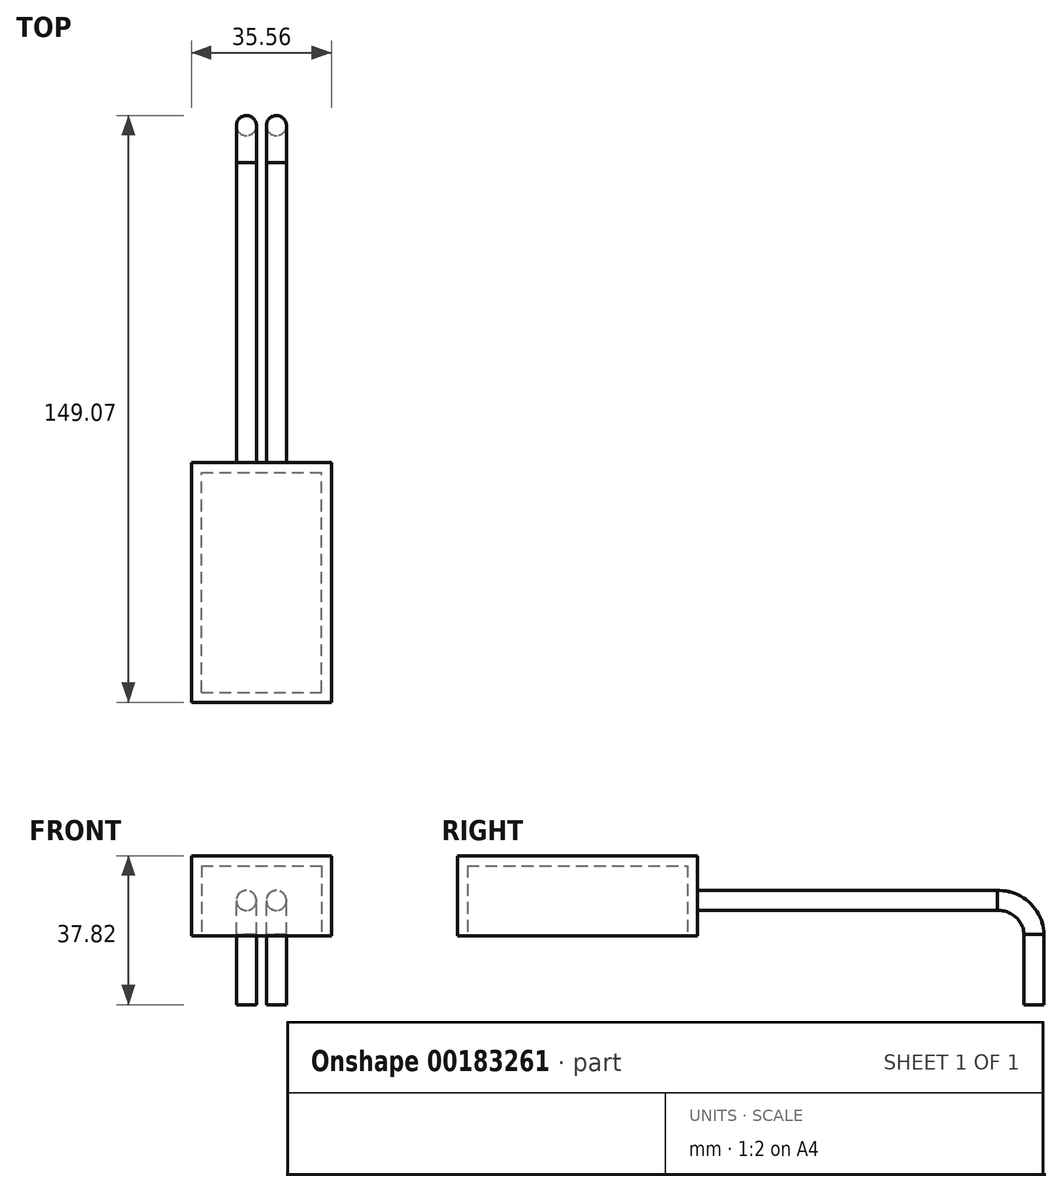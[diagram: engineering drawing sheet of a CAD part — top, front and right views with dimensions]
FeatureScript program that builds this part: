
annotation { "Feature Type Name" : "Feature", "Feature Type Description" : "" }
export const myFeature = defineFeature(function(context is Context, id is Id, definition is map)
    precondition{}
    {
        {
            var Q0;
            Q0=qCreatedBy(makeId("Top.planeOp"),FACE);
            var sketch = newSketch(context, id + "F0", { "sketchPlane" : qUnion([Q0])});
            skLineSegment(sketch, "E0.bottom", {"start": v(0, 0) * mm, "end": v(30.48, 0) * mm});
            skLineSegment(sketch, "E0.top", {"start": v(0, 55.88) * mm, "end": v(30.48, 55.88) * mm});
            skLineSegment(sketch, "E0.left", {"start": v(0, 0) * mm, "end": v(0, 55.88) * mm});
            skLineSegment(sketch, "E0.right", {"start": v(30.48, 0) * mm, "end": v(30.48, 55.88) * mm});
            skLineSegment(sketch, "E1.bottom", {"start": v(-2.54, -2.54) * mm, "end": v(33.02, -2.54) * mm});
            skLineSegment(sketch, "E1.top", {"start": v(-2.54, 58.42) * mm, "end": v(33.02, 58.42) * mm});
            skLineSegment(sketch, "E1.left", {"start": v(-2.54, -2.54) * mm, "end": v(-2.54, 58.42) * mm});
            skLineSegment(sketch, "E1.right", {"start": v(33.02, -2.54) * mm, "end": v(33.02, 58.42) * mm});
            skLineSegment(sketch, "E2.bottom", {"start": v(22.16, 0) * mm, "end": v(22.47, 0) * mm});
            skLineSegment(sketch, "E2.top", {"start": v(22.16, -2.54) * mm, "end": v(22.47, -2.54) * mm});
            skSolve(sketch);
        }
        {
            var Q0;
            Q0=makeQuery(id+"F0.imprint","IMPRINT",FACE,{"disambiguationData":[TD([[makeQuery(id+"F0.imprint","IMPRINT",EDGE,{"derivedFrom":sQuery(id+"F0.wireOp",EDGE,"E0.top")}),1.0]])]});
            extrude(context, id + "F1", {"entities" : qUnion([Q0]), "depth" : 20.32 * mm});
        }
        {
            var Q0;
            Q0=makeQuery(id+"F1.opExtrude","CAP_FACE",FACE,{"disambiguationData":[OSD([sQuery(id+"F0.wireOp",EDGE,"E0.bottom"),sQuery(id+"F0.wireOp",EDGE,"E0.top"),sQuery(id+"F0.wireOp",EDGE,"E0.left"),sQuery(id+"F0.wireOp",EDGE,"E0.right"),sQuery(id+"F0.wireOp",EDGE,"E1.bottom"),sQuery(id+"F0.wireOp",EDGE,"E1.top"),sQuery(id+"F0.wireOp",EDGE,"E1.left"),sQuery(id+"F0.wireOp",EDGE,"E1.right"),sQuery(id+"F0.wireOp",EDGE,"E2.bottom"),sQuery(id+"F0.wireOp",EDGE,"E2.top")])],"isStart":false});
            var sketch = newSketch(context, id + "F2", { "sketchPlane" : qUnion([Q0])});
            skLineSegment(sketch, "E3.bottom", {"start": v(-2.54, -2.54) * mm, "end": v(33.02, -2.54) * mm});
            skLineSegment(sketch, "E3.top", {"start": v(-2.54, 58.42) * mm, "end": v(33.02, 58.42) * mm});
            skLineSegment(sketch, "E3.left", {"start": v(-2.54, -2.54) * mm, "end": v(-2.54, 58.42) * mm});
            skLineSegment(sketch, "E3.right", {"start": v(33.02, -2.54) * mm, "end": v(33.02, 58.42) * mm});
            skSolve(sketch);
        }
        {
            var Q0;
            Q0=makeQuery(id+"F2.imprint","IMPRINT",FACE,{"disambiguationData":[TD([[makeQuery(id+"F2.imprint","IMPRINT",EDGE,{"derivedFrom":makeQuery(id+"F1.opExtrude","CAP_EDGE",EDGE,{"disambiguationData":[OSD([sQuery(id+"F0.wireOp",EDGE,"E0.top")])],"isStart":false})}),-1.0]])]});
            extrude(context, id + "F3", {"entities" : qUnion([Q0]), "operationType" : NewBodyOperationType.ADD, "oppositeDirection" : true, "depth" : 2.54 * mm});
        }
        {
            var Q0;
            Q0=makeQuery(id+"F1.opExtrude","SWEPT_FACE",FACE,{"disambiguationData":[OSD([sQuery(id+"F0.wireOp",EDGE,"E1.top")])]});
            var sketch = newSketch(context, id + "F4", { "sketchPlane" : qUnion([Q0])});
            skCircle(sketch, "E4", {"center": v(-11.43, 8.95) * mm, "radius": 2.54 * mm});
            skCircle(sketch, "E5", {"center": v(-19.05, 8.95) * mm, "radius": 2.54 * mm});
            skSolve(sketch);
        }
        {
            var Q0;
            Q0=qCreatedBy(makeId("Right.planeOp"),FACE);
            var sketch = newSketch(context, id + "F5", { "sketchPlane" : qUnion([Q0])});
            skLineSegment(sketch, "E6", {"start": v(58.83, 9.09) * mm, "end": v(135.03, 9.09) * mm});
            skLineSegment(sketch, "E7", {"start": v(135.03, 9.09) * mm, "end": v(135.03, 0) * mm, "construction": true});
            skArc(sketch, "E8", {"start": v(144.12, 0) * mm, "mid": v(141.46, 6.43) * mm, "end": v(135.03, 9.09) * mm});
            skLineSegment(sketch, "E9", {"start": v(144.12, 0) * mm, "end": v(144.12, -17.92) * mm});
            skLineSegment(sketch, "E10", {"start": v(58.42, 0) * mm, "end": v(58.42, 16.15) * mm, "construction": true});
            skLineSegment(sketch, "E11", {"start": v(58.83, 9.09) * mm, "end": v(58.42, 9.09) * mm});
            skSolve(sketch);
        }
        {
            var Q0;
            Q0=makeQuery(id+"F4.imprint","IMPRINT",FACE,{"disambiguationData":[TD([[makeQuery(id+"F4.imprint","IMPRINT",EDGE,{"derivedFrom":sQuery(id+"F4.wireOp",EDGE,"E5")}),1.0]])]});
            var Q1;
            Q1=makeQuery(id+"F4.imprint","IMPRINT",FACE,{"disambiguationData":[TD([[makeQuery(id+"F4.imprint","IMPRINT",EDGE,{"derivedFrom":sQuery(id+"F4.wireOp",EDGE,"E4")}),1.0]])]});
            var Q2;
            Q2=sQuery(id+"F5.wireOp",EDGE,"E8");
            var Q3;
            Q3=sQuery(id+"F5.wireOp",EDGE,"E6");
            var Q4;
            Q4=sQuery(id+"F5.wireOp",EDGE,"E9");
            sweep(context, id + "F6", {"operationType" : NewBodyOperationType.ADD, "profiles" : qUnion([Q0, Q1]), "path" : qUnion([Q2, Q3, Q4])});
        }
    });
